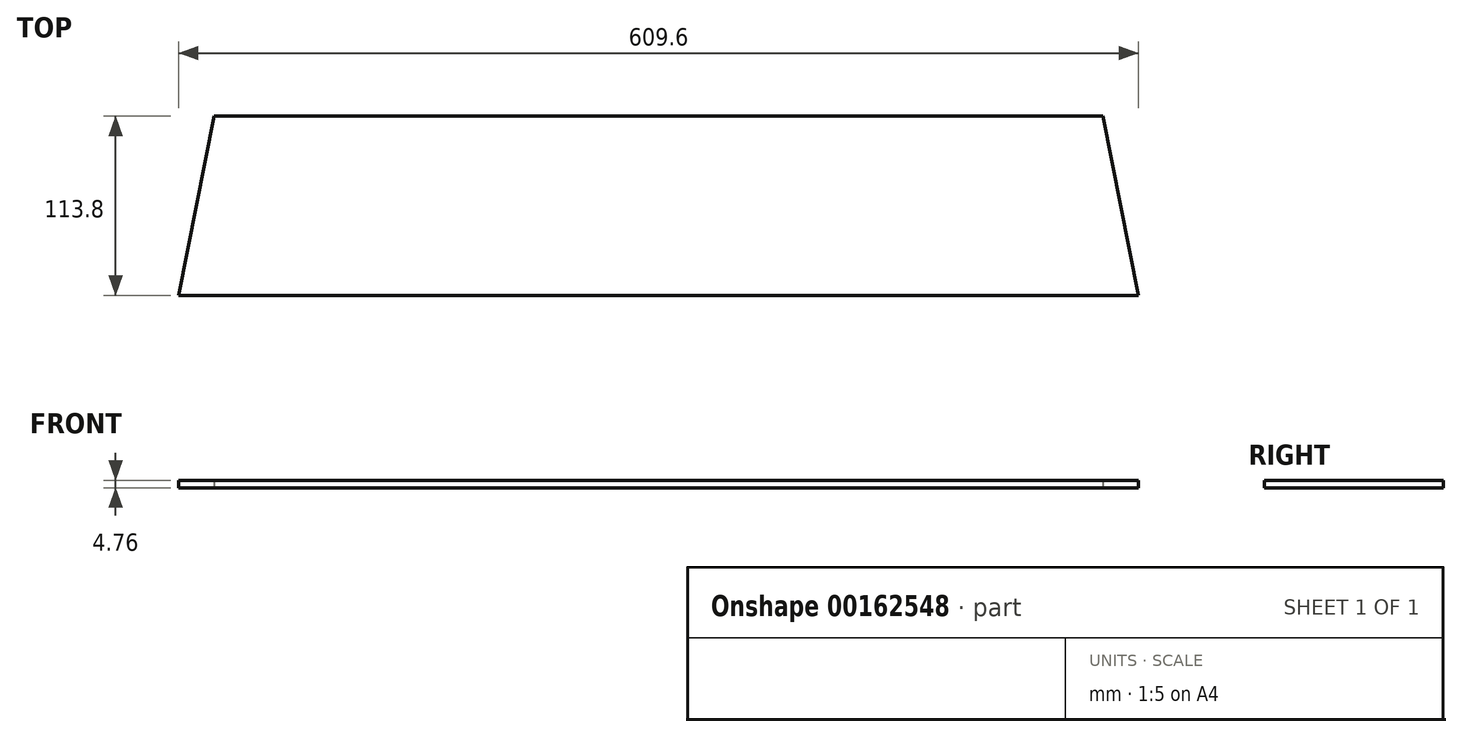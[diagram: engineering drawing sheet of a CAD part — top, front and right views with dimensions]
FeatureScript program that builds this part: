
annotation { "Feature Type Name" : "Feature", "Feature Type Description" : "" }
export const myFeature = defineFeature(function(context is Context, id is Id, definition is map)
    precondition{}
    {
        {
            var Q0;
            Q0=qCreatedBy(makeId("Top.planeOp"),FACE);
            var sketch = newSketch(context, id + "F0", { "sketchPlane" : qUnion([Q0])});
            skLineSegment(sketch, "E0.bottom", {"start": v(314.1, 56.9) * mm, "end": v(-250.7, 56.9) * mm});
            skLineSegment(sketch, "E0.top", {"start": v(336.5, -56.9) * mm, "end": v(-273.1, -56.9) * mm});
            skPoint(sketch, "E0.middle", {"position": v(0, 0) * mm});
            skLineSegment(sketch, "E1", {"start": v(-273.1, -56.9) * mm, "end": v(-250.7, 56.9) * mm});
            skLineSegment(sketch, "E2", {"start": v(336.5, -56.9) * mm, "end": v(314.1, 56.9) * mm});
            skPoint(sketch, "E0.right.start.orphan", {"position": v(-336.5, 56.9) * mm});
            skPoint(sketch, "E0.left.start.orphan", {"position": v(273.1, 56.9) * mm});
            skSolve(sketch);
        }
        {
            var Q0;
            Q0=qSketchRegion(id+"F0",true);
            extrude(context, id + "F1", {"entities" : qUnion([Q0]), "depth" : 4.76 * mm});
        }
    });
